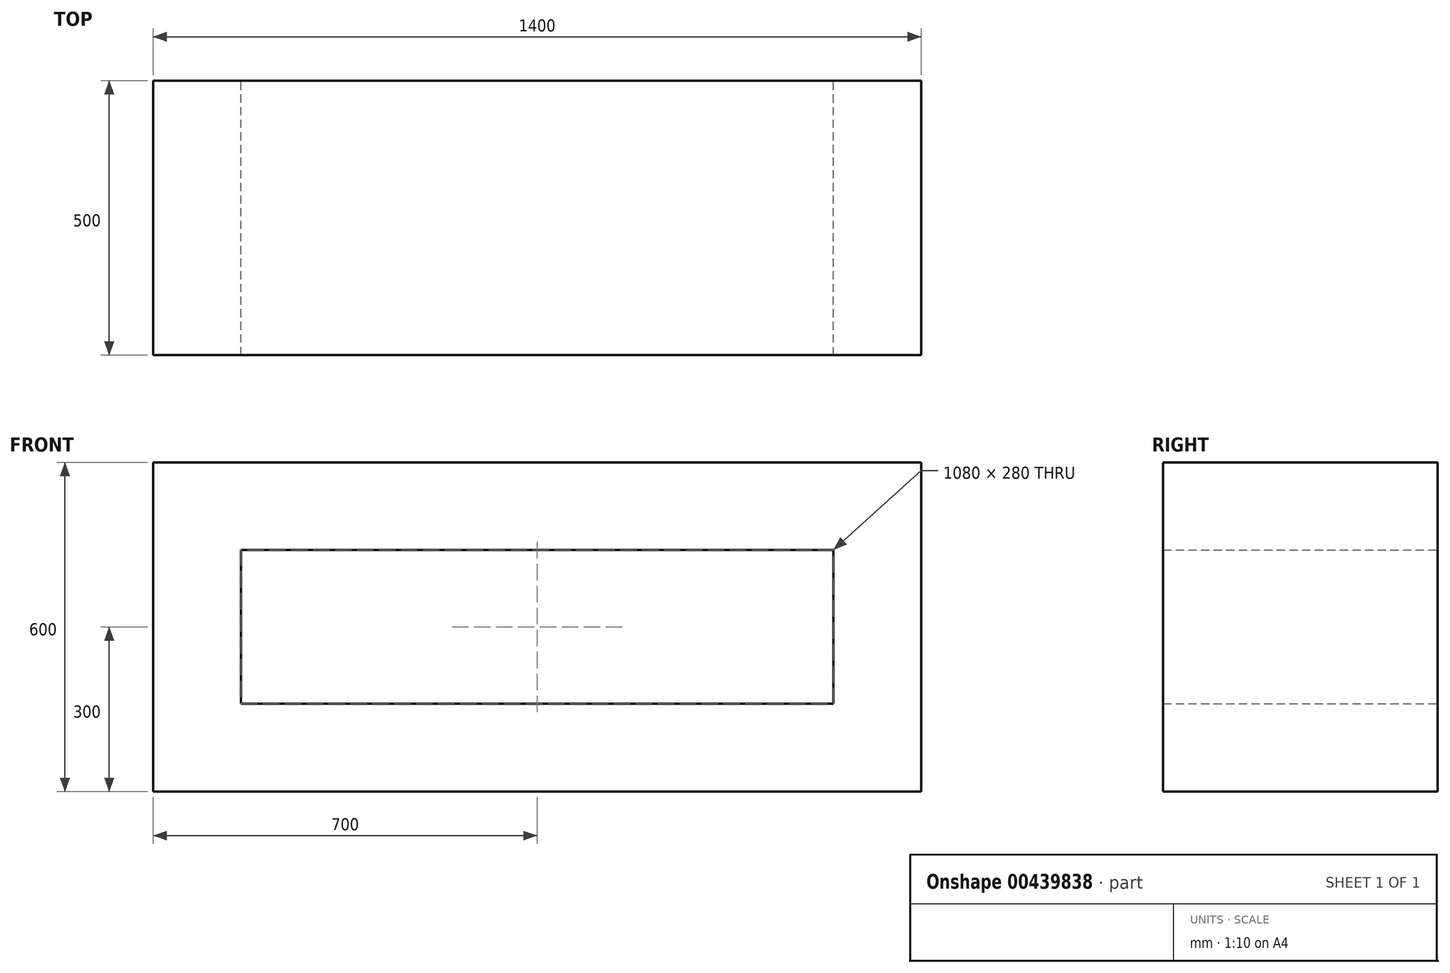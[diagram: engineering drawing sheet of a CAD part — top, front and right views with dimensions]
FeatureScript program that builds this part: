
annotation { "Feature Type Name" : "Feature", "Feature Type Description" : "" }
export const myFeature = defineFeature(function(context is Context, id is Id, definition is map)
    precondition{}
    {
        {
            var Q0;
            Q0=qCreatedBy(makeId("Front.planeOp"),FACE);
            var sketch = newSketch(context, id + "F0", { "sketchPlane" : qUnion([Q0])});
            skLineSegment(sketch, "E0.bottom", {"start": v(0, 0) * mm, "end": v(1400, 0) * mm});
            skLineSegment(sketch, "E0.top", {"start": v(0, 600) * mm, "end": v(1400, 600) * mm});
            skLineSegment(sketch, "E0.left", {"start": v(0, 0) * mm, "end": v(0, 600) * mm});
            skLineSegment(sketch, "E0.right", {"start": v(1400, 0) * mm, "end": v(1400, 600) * mm});
            skLineSegment(sketch, "E1.bottom", {"start": v(160, 440) * mm, "end": v(1240, 440) * mm});
            skLineSegment(sketch, "E1.top", {"start": v(160, 160) * mm, "end": v(1240, 160) * mm});
            skLineSegment(sketch, "E1.left", {"start": v(160, 440) * mm, "end": v(160, 160) * mm});
            skLineSegment(sketch, "E1.right", {"start": v(1240, 440) * mm, "end": v(1240, 160) * mm});
            skSolve(sketch);
        }
        {
            var Q0;
            Q0=makeQuery(id+"F0.imprint","IMPRINT",FACE,{"disambiguationData":[TD([[makeQuery(id+"F0.imprint","IMPRINT",EDGE,{"derivedFrom":sQuery(id+"F0.wireOp",EDGE,"E0.bottom")}),1.0]])]});
            extrude(context, id + "F1", {"entities" : qUnion([Q0]), "depth" : 420 * mm});
        }
        {
            var Q0;
            Q0=makeQuery(id+"F1.opExtrude","CAP_FACE",FACE,{"disambiguationData":[OSD([sQuery(id+"F0.wireOp",EDGE,"E0.bottom"),sQuery(id+"F0.wireOp",EDGE,"E0.top"),sQuery(id+"F0.wireOp",EDGE,"E0.left"),sQuery(id+"F0.wireOp",EDGE,"E0.right"),sQuery(id+"F0.wireOp",EDGE,"E1.bottom"),sQuery(id+"F0.wireOp",EDGE,"E1.top"),sQuery(id+"F0.wireOp",EDGE,"E1.left"),sQuery(id+"F0.wireOp",EDGE,"E1.right")])],"isStart":false});
            extrude(context, id + "F2", {"entities" : qUnion([Q0]), "operationType" : NewBodyOperationType.ADD, "depth" : 80 * mm});
        }
    });
